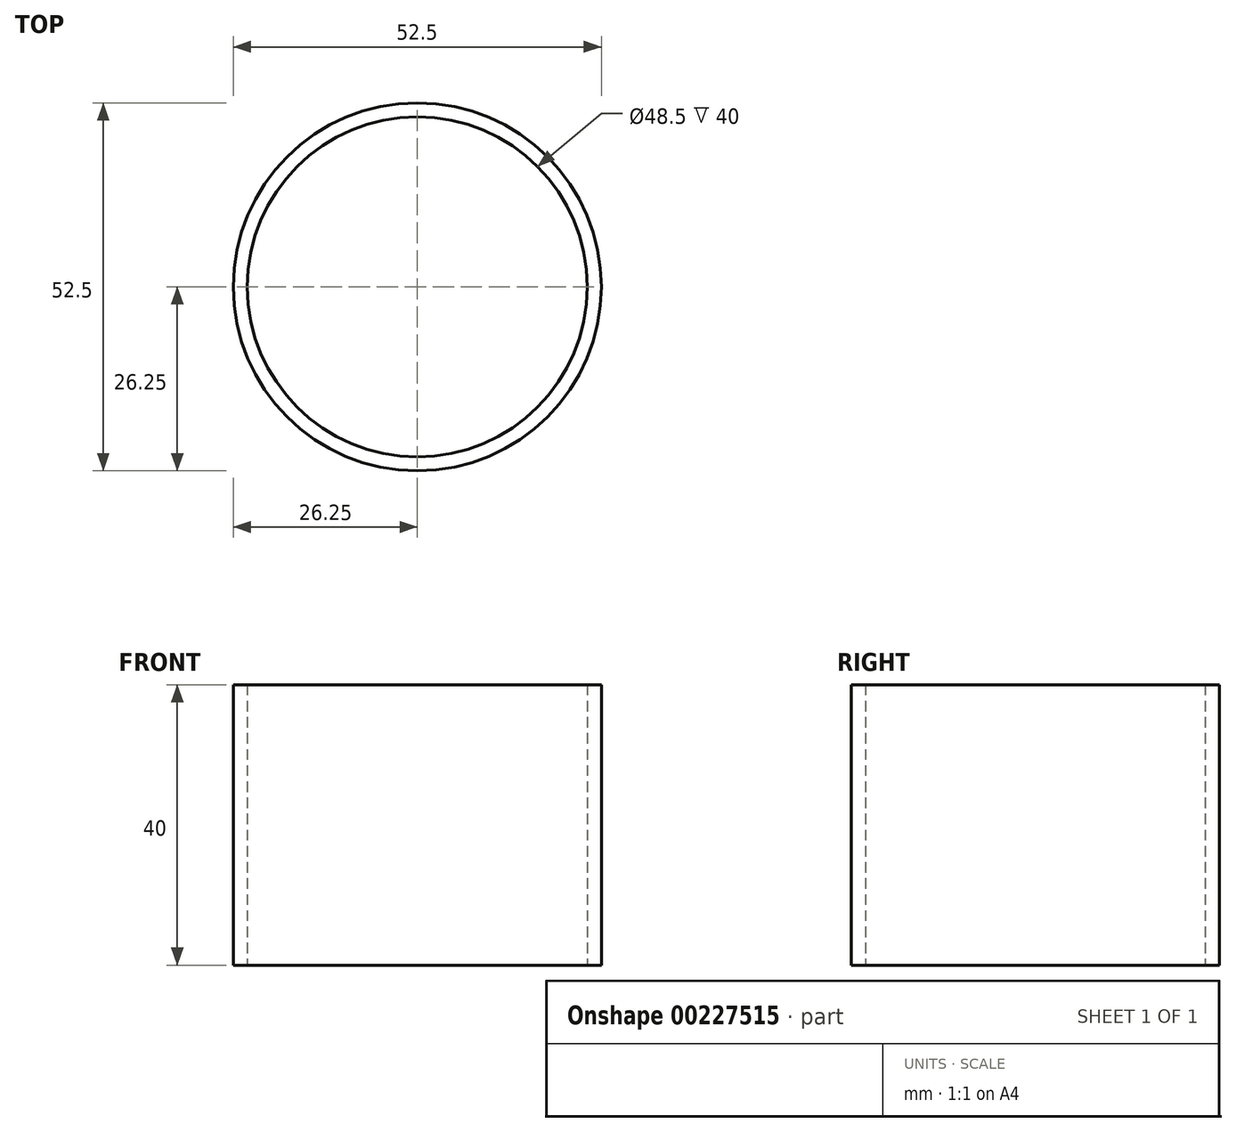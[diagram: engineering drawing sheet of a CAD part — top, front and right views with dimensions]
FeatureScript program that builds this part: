
annotation { "Feature Type Name" : "Feature", "Feature Type Description" : "" }
export const myFeature = defineFeature(function(context is Context, id is Id, definition is map)
    precondition{}
    {
        {
            var Q0;
            Q0=qCreatedBy(makeId("Top.planeOp"),FACE);
            var sketch = newSketch(context, id + "F0", { "sketchPlane" : qUnion([Q0])});
            skCircle(sketch, "E0", {"center": v(0, 0) * mm, "radius": 24.25 * mm});
            skCircle(sketch, "E1", {"center": v(0, 0) * mm, "radius": 26.25 * mm});
            skCircle(sketch, "E2", {"center": v(0, 0) * mm, "radius": 29.25 * mm});
            skSolve(sketch);
        }
        {
            var Q0;
            Q0=makeQuery(id+"F0.imprint","IMPRINT",FACE,{"disambiguationData":[TD([[makeQuery(id+"F0.imprint","IMPRINT",EDGE,{"derivedFrom":sQuery(id+"F0.wireOp",EDGE,"E0")}),-1.0]])]});
            extrude(context, id + "F1", {"entities" : qUnion([Q0]), "depth" : 40 * mm});
        }
    });
